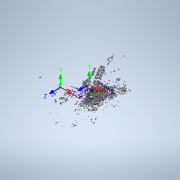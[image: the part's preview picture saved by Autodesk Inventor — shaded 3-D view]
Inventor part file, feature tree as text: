
AUTODESK INVENTOR PART (.ipt)
format: ipt  version: 2021 (Build 250183000, 183)  size: 3,845,632 bytes
history: native  units: mm
features: other x23, sketch x2, extrude x1, projected_geometry x1, surface_op x1
ambient origin geometry x8: Origin, YZ Plane, XZ Plane, XY Plane, X Axis, Y Axis, Z Axis, Center Point
feature tree (28):
  other  "Sólido1"
  other  "leonOSM"
  other  "SCU1"
  extrude  "Extrusión1"  Depth=1000.0mm TaperAngle=0.0deg
  other  "SCU2"
  sketch  "Boceto4"  dims[d14=1500000.0mm d15=2200000.0mm d17=1630000.0mm d18=1000000.0mm d19=850000.0mm d25=1500000.0mm d26=2000000.0mm d27=1171781.0mm d28=10500.0mm d29=-1640766.0mm d30=0.0mm d31=0.0mm d32=0.0mm d33=260000.0mm d34=380000.0mm d35=350000.0mm d36=1180000.0mm d37=220000.0mm d38=320000.0mm d39=420000.0mm d40=375000.0mm d41=514000.0mm d42=340000.0mm d43=350000.0mm d44=445000.0mm]
  sketch  "Boceto1"  dims[d0=0.0mm d1=0.0mm d2=0.0mm d3=0.0mm d4=0.0mm d5=0.0mm d10=1000.0mm d11=0.0mm]
  projected_geometry  "Contorno proyectado1"
  other  "BuildingEntrance"
  other  "Building"
  other  "Pool"
  other  "SoccerPitch"
  other  "RoadArea"
  surface_op  "SurfaceArea"
  other  "SCU1: Plano YZ"
  other  "SCU1: Plano XZ"
  other  "SCU1: Plano XY"
  other  "SCU1: Eje X"
  other  "SCU1: Eje Y"
  other  "SCU1: Eje Z"
  other  "SCU1: Centro"
  other  "SCU2: Plano YZ"
  other  "SCU2: Plano XZ"
  other  "SCU2: Plano XY"
  other  "SCU2: Eje X"
  other  "SCU2: Eje Y"
  other  "SCU2: Eje Z"
  other  "SCU2: Centro"
